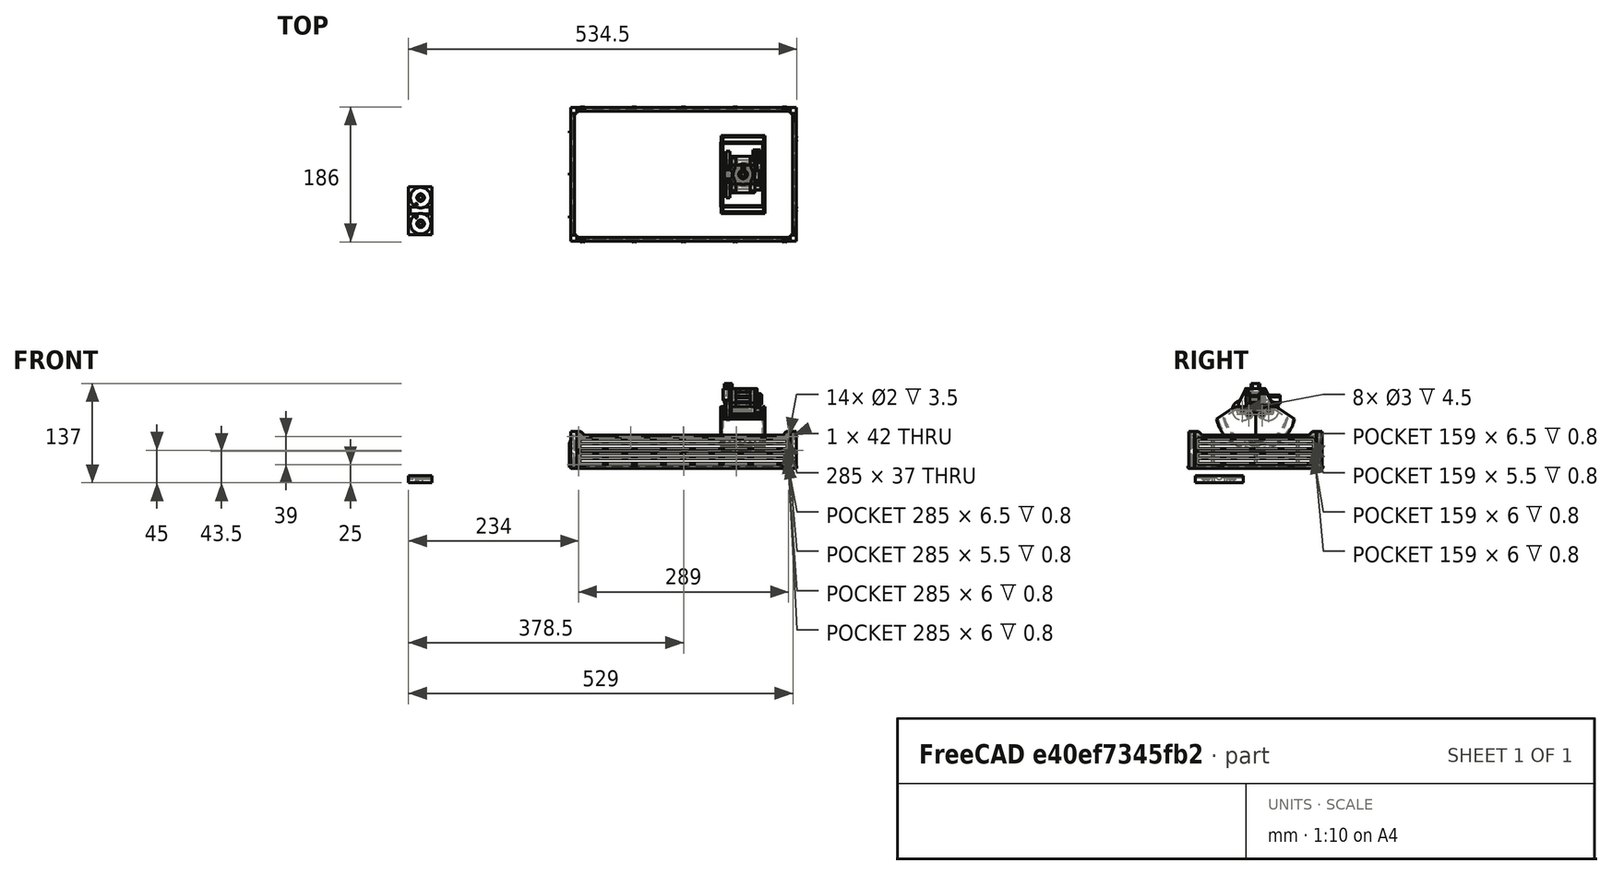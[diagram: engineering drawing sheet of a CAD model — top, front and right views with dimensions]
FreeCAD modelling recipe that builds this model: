
FCSTD DOCUMENT  (FreeCAD 0.18.4R)
Label: bucket
License: All rights reserved
LicenseURL: http://en.wikipedia.org/wiki/All_rights_reserved
objects: Part::Cylinder×157, Part::MultiFuse×80, Part::Cut×78, Part::Box×39, Part::Chamfer×38, Part::Fillet×16, Part::Feature×12, Part::Extrusion×8, Part::Mirroring×4
note: 432 computed .brp shape members not serialized (recipe doc carries the construction recipe); baked Part::Feature solids carry a one-line shape summary decoded from their .brp

FEATURE [Part::Feature] Fusion281001  label="kipper"
  shape: bbox 313 x 186 x 59 mm, 528 faces, 2 solids (baked)
FEATURE [Part::Cylinder] Cylinder002
  Angle = 360
  AttacherType = Attacher::AttachEngine3D
  Height = 5
  Placement = pos=(437,102.5,100) rot=(0,1,0;1.5708rad)
  Radius = 14
FEATURE [Part::Cylinder] Cylinder003
  Angle = 360
  AttacherType = Attacher::AttachEngine3D
  Height = 5
  Placement = pos=(437,67.5,100) rot=(0,1,0;1.5708rad)
  Radius = 14
FEATURE [Part::Cylinder] Cylinder004
  Angle = 360
  AttacherType = Attacher::AttachEngine3D
  Height = 60
  Placement = pos=(432,103,100) rot=(0,1,0;1.5708rad)
  Radius = 1.5
FEATURE [Part::Cylinder] Cylinder005
  Angle = 360
  AttacherType = Attacher::AttachEngine3D
  Height = 60
  Placement = pos=(432,67,100) rot=(0,1,0;1.5708rad)
  Radius = 1.5
FEATURE [Part::Box] Box  label="Cube"
  AttacherType = Attacher::AttachEngine3D
  Height = 10
  Length = 32
  Placement = pos=(446,60,95) rot=(0,0,1;0rad)
  Width = 50
FEATURE [Part::Cylinder] Cylinder1189  label="Cylinder1407"
  Angle = 360
  AttacherType = Attacher::AttachEngine3D
  Height = 27
  Radius = 8
FEATURE [Part::Box] Box501  label="Cube727"
  AttacherType = Attacher::AttachEngine3D
  Height = 27
  Length = 10.4
  Placement = pos=(-5.2,-6.2,0) rot=(0,0,1;0rad)
  Width = 12.4
FEATURE [Part::Cylinder] Cylinder1190  label="Cylinder1408"
  Angle = 360
  AttacherType = Attacher::AttachEngine3D
  Height = 17
  Radius = 8
FEATURE [Part::Cylinder] Cylinder1191  label="Cylinder1409"
  Angle = 360
  AttacherType = Attacher::AttachEngine3D
  Height = 17
  Radius = 6.5
FEATURE [Part::Cut] Cut014239
  Base = -> Cylinder1190
  Refine = true
  Tool = -> Cylinder1191
FEATURE [Part::Fillet] Fillet395
  Base = -> Box501
  Edges = 4 edges r=1: [Edge1,Edge3,Edge5,Edge7]
FEATURE [Part::Cut] Cut014240
  Base = -> Cylinder1189
  Refine = true
  Tool = -> Fillet395
FEATURE [Part::MultiFuse] Fusion248002050121
  Refine = true
  Shapes = -> [Cut014239,Cut014240]
FEATURE [Part::Cylinder] Cylinder1192  label="Cylinder1410"
  Angle = 360
  AttacherType = Attacher::AttachEngine3D
  Height = 27
  Radius = 8
FEATURE [Part::Cut] Cut014241  label="bucket-opening-motor"
  Base = -> Cylinder1192
  Placement = pos=(441.5,85,137) rot=(1,0,0;3.14159rad)
  Refine = true
  Tool = -> Fusion248002050121
FEATURE [Part::Cylinder] Cylinder1193  label="Cylinder1411"
  Angle = 360
  AttacherType = Attacher::AttachEngine3D
  Height = 27
  Radius = 8
FEATURE [Part::Box] Box502  label="Cube728"
  AttacherType = Attacher::AttachEngine3D
  Height = 27
  Length = 10.4
  Placement = pos=(-5.2,-6.2,0) rot=(0,0,1;0rad)
  Width = 12.4
FEATURE [Part::Cylinder] Cylinder1194  label="Cylinder1412"
  Angle = 360
  AttacherType = Attacher::AttachEngine3D
  Height = 17
  Radius = 8
FEATURE [Part::Cylinder] Cylinder1195  label="Cylinder1413"
  Angle = 360
  AttacherType = Attacher::AttachEngine3D
  Height = 17
  Radius = 6.5
FEATURE [Part::Cut] Cut014242
  Base = -> Cylinder1194
  Refine = true
  Tool = -> Cylinder1195
FEATURE [Part::Fillet] Fillet396
  Base = -> Box502
  Edges = 4 edges r=1: [Edge1,Edge3,Edge5,Edge7]
FEATURE [Part::Cut] Cut014243
  Base = -> Cylinder1193
  Refine = true
  Tool = -> Fillet396
FEATURE [Part::MultiFuse] Fusion248002050122
  Refine = true
  Shapes = -> [Cut014242,Cut014243]
FEATURE [Part::Cylinder] Cylinder1196  label="Cylinder1414"
  Angle = 360
  AttacherType = Attacher::AttachEngine3D
  Height = 27
  Radius = 8
FEATURE [Part::Cut] Cut014244  label="bucket-turning-motor"
  Base = -> Cylinder1196
  Placement = pos=(480.5,119,114.75) rot=(1,0,0;1.5708rad)
  Refine = true
  Tool = -> Fusion248002050122
FEATURE [Part::Cylinder] Cylinder1197
  Angle = 360
  AttacherType = Attacher::AttachEngine3D
  Height = 5
  Placement = pos=(462,85,145) rot=(0,0,1;0rad)
  Radius = 14
FEATURE [Part::Cylinder] Cylinder1198
  Angle = 360
  AttacherType = Attacher::AttachEngine3D
  Height = 60
  Placement = pos=(432,94,94) rot=(0,1,0;1.5708rad)
  Radius = 1.5
FEATURE [Part::Cylinder] Cylinder1199
  Angle = 360
  AttacherType = Attacher::AttachEngine3D
  Height = 9.5
  Placement = pos=(434.75,67.5,100) rot=(0,1,0;1.5708rad)
  Radius = 5
FEATURE [Part::Cylinder] Cylinder1200
  Angle = 360
  AttacherType = Attacher::AttachEngine3D
  Height = 9.5
  Placement = pos=(434.75,102.5,100) rot=(0,1,0;1.5708rad)
  Radius = 5
FEATURE [Part::MultiFuse] Fusion
  Placement = pos=(2,-0.5,0) rot=(0,0,1;0rad)
  Refine = true
  Shapes = -> [Cylinder1199,Cylinder003]
FEATURE [Part::MultiFuse] Fusion248002050123
  Placement = pos=(2,0.5,0) rot=(0,0,1;0rad)
  Refine = true
  Shapes = -> [Cylinder002,Cylinder1200]
FEATURE [Part::Cylinder] Cylinder1201
  Angle = 360
  AttacherType = Attacher::AttachEngine3D
  Height = 9.5
  Placement = pos=(462,85,142.75) rot=(0,0,1;0rad)
  Radius = 5
FEATURE [Part::MultiFuse] Fusion248002050124
  Placement = pos=(0,0,-32.75) rot=(0,0,1;0rad)
  Refine = true
  Shapes = -> [Cylinder1197,Cylinder1201]
FEATURE [Part::Cylinder] Cylinder1202
  Angle = 360
  AttacherType = Attacher::AttachEngine3D
  Height = 15
  Placement = pos=(480,92,115) rot=(1,0,0;1.5708rad)
  Radius = 4
FEATURE [Part::Box] Box507  label="Cube733"
  AttacherType = Attacher::AttachEngine3D
  Height = 5
  Length = 22
  Placement = pos=(451,72,125) rot=(0,0,1;0rad)
  Width = 26
FEATURE [Part::Cylinder] Cylinder1203
  Angle = 360
  AttacherType = Attacher::AttachEngine3D
  Height = 10
  Placement = pos=(462,85,110) rot=(0,0,1;0rad)
  Radius = 15
FEATURE [Part::Box] Box508  label="Cube734"
  AttacherType = Attacher::AttachEngine3D
  Height = 10
  Length = 22
  Placement = pos=(462,77,110) rot=(0,0,1;0rad)
  Width = 15
FEATURE [Part::Box] Box506  label="Cube732"
  AttacherType = Attacher::AttachEngine3D
  Height = 25
  Length = 6
  Placement = pos=(472,62,105) rot=(0,0,1;0rad)
  Width = 46
FEATURE [Part::Chamfer] Chamfer005
  Base = -> Box506
  Edges = 2 edges: [Edge10 r1=20 r2=10,Edge12 r1=20 r2=10]
FEATURE [Part::Box] Box509  label="Cube735"
  AttacherType = Attacher::AttachEngine3D
  Height = 25
  Length = 6
  Placement = pos=(472,62,105) rot=(0,0,1;0rad)
  Width = 46
FEATURE [Part::Chamfer] Chamfer006
  Base = -> Box509
  Edges = 2 edges: [Edge10 r1=20 r2=10,Edge12 r1=20 r2=10]
  Placement = pos=(-26,0,0) rot=(0,0,1;0rad)
FEATURE [Part::Cut] Cut014245
  Base = -> Chamfer006
  Refine = true
  Tool = -> Cylinder1203
FEATURE [Part::Cylinder] Cylinder1204  label="Cylinder1415"
  Angle = 360
  AttacherType = Attacher::AttachEngine3D
  Height = 27
  Radius = 8
FEATURE [Part::Box] Box510  label="Cube736"
  AttacherType = Attacher::AttachEngine3D
  Height = 27
  Length = 10.4
  Placement = pos=(-5.2,-6.2,0) rot=(0,0,1;0rad)
  Width = 12.4
FEATURE [Part::Cylinder] Cylinder1205  label="Cylinder1416"
  Angle = 360
  AttacherType = Attacher::AttachEngine3D
  Height = 17
  Radius = 8
FEATURE [Part::Cylinder] Cylinder1206  label="Cylinder1417"
  Angle = 360
  AttacherType = Attacher::AttachEngine3D
  Height = 17
  Radius = 6.5
FEATURE [Part::Cut] Cut014247
  Base = -> Cylinder1205
  Refine = true
  Tool = -> Cylinder1206
FEATURE [Part::Fillet] Fillet398
  Base = -> Box510
  Edges = 4 edges r=1: [Edge1,Edge3,Edge5,Edge7]
FEATURE [Part::Cut] Cut014248
  Base = -> Cylinder1204
  Refine = true
  Tool = -> Fillet398
FEATURE [Part::MultiFuse] Fusion248002050126
  Refine = true
  Shapes = -> [Cut014247,Cut014248]
FEATURE [Part::Cylinder] Cylinder1207  label="Cylinder1418"
  Angle = 360
  AttacherType = Attacher::AttachEngine3D
  Height = 27
  Radius = 8
FEATURE [Part::Cut] Cut014249  label="bucket-opening-motor001"
  Base = -> Cylinder1207
  Placement = pos=(441.5,85,137) rot=(1,0,0;3.14159rad)
  Refine = true
  Tool = -> Fusion248002050126
FEATURE [Part::Cylinder] Cylinder1208  label="Cylinder1419"
  Angle = 360
  AttacherType = Attacher::AttachEngine3D
  Height = 27
  Radius = 8
FEATURE [Part::Box] Box511  label="Cube737"
  AttacherType = Attacher::AttachEngine3D
  Height = 27
  Length = 10.4
  Placement = pos=(-5.2,-6.2,0) rot=(0,0,1;0rad)
  Width = 12.4
FEATURE [Part::Cylinder] Cylinder1209  label="Cylinder1420"
  Angle = 360
  AttacherType = Attacher::AttachEngine3D
  Height = 17
  Radius = 8
FEATURE [Part::Cylinder] Cylinder1210  label="Cylinder1421"
  Angle = 360
  AttacherType = Attacher::AttachEngine3D
  Height = 17
  Radius = 6.5
FEATURE [Part::Cut] Cut014250
  Base = -> Cylinder1209
  Refine = true
  Tool = -> Cylinder1210
FEATURE [Part::Fillet] Fillet399
  Base = -> Box511
  Edges = 4 edges r=1: [Edge1,Edge3,Edge5,Edge7]
FEATURE [Part::Cut] Cut014251
  Base = -> Cylinder1208
  Refine = true
  Tool = -> Fillet399
FEATURE [Part::MultiFuse] Fusion248002050127
  Refine = true
  Shapes = -> [Cut014250,Cut014251]
FEATURE [Part::Cylinder] Cylinder1211  label="Cylinder1422"
  Angle = 360
  AttacherType = Attacher::AttachEngine3D
  Height = 27
  Radius = 8
FEATURE [Part::Cut] Cut014252  label="bucket-turning-motor001"
  Base = -> Cylinder1211
  Placement = pos=(480.5,119,114.75) rot=(1,0,0;1.5708rad)
  Refine = true
  Tool = -> Fusion248002050127
FEATURE [Part::Box] Box513  label="Cube739"
  AttacherType = Attacher::AttachEngine3D
  Height = 21
  Length = 6
  Placement = pos=(441,77.5,109) rot=(0,0,1;0rad)
  Width = 15
FEATURE [Part::Cylinder] Cylinder1212
  Angle = 360
  AttacherType = Attacher::AttachEngine3D
  Height = 15
  Placement = pos=(441.5,85,94) rot=(0,0,1;0rad)
  Radius = 4.75
FEATURE [Part::Cylinder] Cylinder1213
  Angle = 360
  AttacherType = Attacher::AttachEngine3D
  Height = 16
  Placement = pos=(441.5,85,94) rot=(0,0,1;0rad)
  Radius = 5.5
FEATURE [Part::Cut] Cut014255
  Base = -> Cut014245
  Refine = true
  Tool = -> Cylinder1213
FEATURE [Part::Cylinder] Cylinder1214
  Angle = 360
  AttacherType = Attacher::AttachEngine3D
  Height = 16
  Placement = pos=(441.5,85,94) rot=(0,0,1;0rad)
  Radius = 5.5
FEATURE [Part::Chamfer] Chamfer007
  Base = -> Box513
  Edges = 2 edges r=1.5: [Edge9,Edge11]
FEATURE [Part::Cylinder] Cylinder1215
  Angle = 360
  AttacherType = Attacher::AttachEngine3D
  Height = 16
  Placement = pos=(441.5,85,94) rot=(0,0,1;0rad)
  Radius = 2
FEATURE [Part::Cut] Cut014257
  Base = -> Chamfer007
  Refine = true
  Tool = -> Cylinder1215
FEATURE [Part::MultiFuse] Fusion248002050128
  Refine = true
  Shapes = -> [Cut014255,Cut014257]
FEATURE [Part::Cut] Cut014258
  Base = -> Fusion248002050128
  Refine = true
  Tool = -> Cut014249
FEATURE [Part::Cylinder] Cylinder1216
  Angle = 360
  AttacherType = Attacher::AttachEngine3D
  Height = 10
  Placement = pos=(462,85,110) rot=(0,0,1;0rad)
  Radius = 15
FEATURE [Part::Cut] Cut014259
  Base = -> Chamfer005
  Refine = true
  Tool = -> Cylinder1216
FEATURE [Part::Cut] Cut014260
  Base = -> Cut014259
  Refine = true
  Tool = -> Box508
FEATURE [Part::Cut] Cut014261
  Base = -> Cut014260
  Refine = true
  Tool = -> Cut014252
FEATURE [Part::Cylinder] Cylinder1217
  Angle = 360
  AttacherType = Attacher::AttachEngine3D
  Height = 15
  Placement = pos=(480,87,115) rot=(1,0,0;1.5708rad)
  Radius = 1.6
FEATURE [Part::MultiFuse] Fusion248002050129
  Placement = pos=(0.5,0,0) rot=(0,0,1;0rad)
  Refine = true
  Shapes = -> [Cylinder1202,Cylinder1217]
FEATURE [Part::Box] Box514  label="Cube740"
  AttacherType = Attacher::AttachEngine3D
  Height = 12
  Length = 7.5
  Placement = pos=(478,72,109) rot=(0,0,1;0rad)
  Width = 5
FEATURE [Part::Cylinder] Cylinder1218
  Angle = 360
  AttacherType = Attacher::AttachEngine3D
  Height = 5
  Placement = pos=(480.5,77,115) rot=(1,0,0;1.5708rad)
  Radius = 3.1
FEATURE [Part::Box] Box515  label="Cube741"
  AttacherType = Attacher::AttachEngine3D
  Height = 21
  Length = 6
  Placement = pos=(441,77.5,109) rot=(0,0,1;0rad)
  Width = 15
FEATURE [Part::Box] Box516  label="Cube742"
  AttacherType = Attacher::AttachEngine3D
  Height = 16
  Length = 3
  Placement = pos=(443,71.5,114) rot=(0,0,1;0rad)
  Width = 27
FEATURE [Part::Cylinder] Cylinder1219  label="Cylinder1423"
  Angle = 360
  AttacherType = Attacher::AttachEngine3D
  Height = 27
  Radius = 8
FEATURE [Part::Box] Box517  label="Cube743"
  AttacherType = Attacher::AttachEngine3D
  Height = 27
  Length = 10.4
  Placement = pos=(-5.2,-6.2,0) rot=(0,0,1;0rad)
  Width = 12.4
FEATURE [Part::Cylinder] Cylinder1220  label="Cylinder1424"
  Angle = 360
  AttacherType = Attacher::AttachEngine3D
  Height = 17
  Radius = 8
FEATURE [Part::Cylinder] Cylinder1221  label="Cylinder1425"
  Angle = 360
  AttacherType = Attacher::AttachEngine3D
  Height = 17
  Radius = 6.5
FEATURE [Part::Cut] Cut014263
  Base = -> Cylinder1220
  Refine = true
  Tool = -> Cylinder1221
FEATURE [Part::Fillet] Fillet401
  Base = -> Box517
  Edges = 4 edges r=1: [Edge1,Edge3,Edge5,Edge7]
FEATURE [Part::Cut] Cut014264
  Base = -> Cylinder1219
  Refine = true
  Tool = -> Fillet401
FEATURE [Part::MultiFuse] Fusion248002050131
  Refine = true
  Shapes = -> [Cut014263,Cut014264]
FEATURE [Part::Cylinder] Cylinder1222  label="Cylinder1426"
  Angle = 360
  AttacherType = Attacher::AttachEngine3D
  Height = 27
  Radius = 8
FEATURE [Part::Cut] Cut014265  label="bucket-opening-motor002"
  Base = -> Cylinder1222
  Placement = pos=(441.5,85,137) rot=(1,0,0;3.14159rad)
  Refine = true
  Tool = -> Fusion248002050131
FEATURE [Part::MultiFuse] Fusion248002050132
  Refine = true
  Shapes = -> [Box515,Cut014265]
FEATURE [Part::Box] Box518  label="Cube744"
  AttacherType = Attacher::AttachEngine3D
  Height = 16
  Length = 12
  Placement = pos=(434,76.5,114) rot=(0,0,1;0rad)
  Width = 17
FEATURE [Part::Cylinder] Cylinder1223
  Angle = 360
  AttacherType = Attacher::AttachEngine3D
  Height = 11
  Placement = pos=(439,96,121) rot=(0,1,0;1.5708rad)
  Radius = 1.2
FEATURE [Part::Cylinder] Cylinder1224
  Angle = 360
  AttacherType = Attacher::AttachEngine3D
  Height = 11
  Placement = pos=(439,74,121) rot=(0,1,0;1.5708rad)
  Radius = 1.2
FEATURE [Part::Cylinder] Cylinder1225
  Angle = 360
  AttacherType = Attacher::AttachEngine3D
  Height = 11
  Placement = pos=(439,74,121) rot=(0,1,0;1.5708rad)
  Radius = 1
FEATURE [Part::Cylinder] Cylinder1226
  Angle = 360
  AttacherType = Attacher::AttachEngine3D
  Height = 11
  Placement = pos=(439,96,121) rot=(0,1,0;1.5708rad)
  Radius = 1
FEATURE [Part::MultiFuse] Fusion248002050134
  Placement = pos=(0,0,-4) rot=(0,0,1;0rad)
  Refine = true
  Shapes = -> [Cylinder1224,Cylinder1223]
FEATURE [Part::MultiFuse] Fusion248002050135
  Refine = true
  Shapes = -> [Cylinder1225,Cylinder1226]
FEATURE [Part::Box] Box519  label="Cube745"
  AttacherType = Attacher::AttachEngine3D
  Height = 16
  Length = 9.5
  Placement = pos=(478,90,107) rot=(0,0,1;0rad)
  Width = 18
FEATURE [Part::Cylinder] Cylinder1228
  Angle = 360
  AttacherType = Attacher::AttachEngine3D
  Height = 11
  Placement = pos=(476,96,128) rot=(0,1,0;1.5708rad)
  Radius = 1.2
FEATURE [Part::Cylinder] Cylinder1229
  Angle = 360
  AttacherType = Attacher::AttachEngine3D
  Height = 11
  Placement = pos=(476,95,105) rot=(0,1,0;1.5708rad)
  Radius = 1.2
FEATURE [Part::Cylinder] Cylinder1230
  Angle = 360
  AttacherType = Attacher::AttachEngine3D
  Height = 15
  Placement = pos=(480,92,115) rot=(1,0,0;1.5708rad)
  Radius = 5.5
FEATURE [Part::Cylinder] Cylinder1231  label="Cylinder1427"
  Angle = 360
  AttacherType = Attacher::AttachEngine3D
  Height = 27
  Radius = 8
FEATURE [Part::Box] Box520  label="Cube746"
  AttacherType = Attacher::AttachEngine3D
  Height = 27
  Length = 10.4
  Placement = pos=(-5.2,-6.2,0) rot=(0,0,1;0rad)
  Width = 12.4
FEATURE [Part::Cylinder] Cylinder1232  label="Cylinder1428"
  Angle = 360
  AttacherType = Attacher::AttachEngine3D
  Height = 17
  Radius = 8
FEATURE [Part::Cylinder] Cylinder1233  label="Cylinder1429"
  Angle = 360
  AttacherType = Attacher::AttachEngine3D
  Height = 17
  Radius = 6.5
FEATURE [Part::Cut] Cut014270
  Base = -> Cylinder1232
  Refine = true
  Tool = -> Cylinder1233
FEATURE [Part::Fillet] Fillet403
  Base = -> Box520
  Edges = 4 edges r=1: [Edge1,Edge3,Edge5,Edge7]
FEATURE [Part::Cut] Cut014271
  Base = -> Cylinder1231
  Refine = true
  Tool = -> Fillet403
FEATURE [Part::MultiFuse] Fusion248002050137
  Refine = true
  Shapes = -> [Cut014270,Cut014271]
FEATURE [Part::Cylinder] Cylinder1234  label="Cylinder1430"
  Angle = 360
  AttacherType = Attacher::AttachEngine3D
  Height = 27
  Radius = 8
FEATURE [Part::Cut] Cut014272  label="bucket-turning-motor002"
  Base = -> Cylinder1234
  Placement = pos=(480.5,119,114.75) rot=(1,0,0;1.5708rad)
  Refine = true
  Tool = -> Fusion248002050137
FEATURE [Part::Cylinder] Cylinder1235
  Angle = 360
  AttacherType = Attacher::AttachEngine3D
  Height = 5
  Placement = pos=(473,95,105) rot=(0,1,0;1.5708rad)
  Radius = 1
FEATURE [Part::Box] Box521  label="Cube747"
  AttacherType = Attacher::AttachEngine3D
  Height = 6
  Length = 5
  Placement = pos=(434,78,42) rot=(0,0,1;0rad)
  Width = 20
FEATURE [Part::Cylinder] Cylinder1243
  Angle = 80
  AttacherType = Attacher::AttachEngine3D
  Height = 60
  Placement = pos=(432,85,100) rot=(0,1,0;1.5708rad)
  Radius = 55
FEATURE [Part::Box] Box522  label="Cube748"
  AttacherType = Attacher::AttachEngine3D
  Height = 6
  Length = 10
  Placement = pos=(434,65,44.75) rot=(0,0,1;0rad)
  Width = 20
FEATURE [Part::MultiFuse] Fusion248002050143
  Refine = true
  Shapes = -> [Box522,Cylinder1243]
FEATURE [Part::Cut] Cut014276
  Base = -> Box521
  Refine = true
  Tool = -> Fusion248002050143
FEATURE [Part::Chamfer] Chamfer012
  Base = -> Cut014276
  Edges = 1 edges: [Edge17 r1=3 r2=8]
FEATURE [Part::Chamfer] Chamfer013
  Base = -> Chamfer012
  Edges = 1 edges: [Edge15 r1=11 r2=2]
  Placement = pos=(1,0,9) rot=(0,0,1;0rad)
FEATURE [Part::Box] Box523  label="Cube749"
  AttacherType = Attacher::AttachEngine3D
  Height = 6
  Length = 5
  Placement = pos=(434,78,42) rot=(0,0,1;0rad)
  Width = 20
FEATURE [Part::Cylinder] Cylinder1244
  Angle = 80
  AttacherType = Attacher::AttachEngine3D
  Height = 60
  Placement = pos=(432,85,100) rot=(0,1,0;1.5708rad)
  Radius = 55
FEATURE [Part::Box] Box524  label="Cube750"
  AttacherType = Attacher::AttachEngine3D
  Height = 6
  Length = 10
  Placement = pos=(434,65,44.75) rot=(0,0,1;0rad)
  Width = 20
FEATURE [Part::MultiFuse] Fusion248002050144
  Refine = true
  Shapes = -> [Box524,Cylinder1244]
FEATURE [Part::Cut] Cut014277
  Base = -> Box523
  Refine = true
  Tool = -> Fusion248002050144
FEATURE [Part::Chamfer] Chamfer014
  Base = -> Cut014277
  Edges = 1 edges: [Edge17 r1=3 r2=8]
FEATURE [Part::Chamfer] Chamfer015
  Base = -> Chamfer014
  Edges = 1 edges: [Edge15 r1=11 r2=2]
  Placement = pos=(29,0,9) rot=(0,0,1;0rad)
FEATURE [Part::Box] Box525  label="Cube751"
  AttacherType = Attacher::AttachEngine3D
  Height = 6
  Length = 5
  Placement = pos=(434,78,42) rot=(0,0,1;0rad)
  Width = 20
FEATURE [Part::Cylinder] Cylinder1245
  Angle = 80
  AttacherType = Attacher::AttachEngine3D
  Height = 60
  Placement = pos=(432,85,100) rot=(0,1,0;1.5708rad)
  Radius = 55
FEATURE [Part::Box] Box526  label="Cube752"
  AttacherType = Attacher::AttachEngine3D
  Height = 6
  Length = 10
  Placement = pos=(434,65,44.75) rot=(0,0,1;0rad)
  Width = 20
FEATURE [Part::MultiFuse] Fusion248002050145
  Refine = true
  Shapes = -> [Box526,Cylinder1245]
FEATURE [Part::Cut] Cut014278
  Base = -> Box525
  Refine = true
  Tool = -> Fusion248002050145
FEATURE [Part::Chamfer] Chamfer016
  Base = -> Cut014278
  Edges = 1 edges: [Edge17 r1=3 r2=8]
FEATURE [Part::Chamfer] Chamfer017
  Base = -> Chamfer016
  Edges = 1 edges: [Edge15 r1=11 r2=2]
  Placement = pos=(15,0,9) rot=(0,0,1;0rad)
FEATURE [Part::Box] Box527  label="Cube753"
  AttacherType = Attacher::AttachEngine3D
  Height = 6
  Length = 5
  Placement = pos=(434,78,42) rot=(0,0,1;0rad)
  Width = 20
FEATURE [Part::Cylinder] Cylinder1246
  Angle = 80
  AttacherType = Attacher::AttachEngine3D
  Height = 60
  Placement = pos=(432,85,100) rot=(0,1,0;1.5708rad)
  Radius = 55
FEATURE [Part::Box] Box528  label="Cube754"
  AttacherType = Attacher::AttachEngine3D
  Height = 6
  Length = 10
  Placement = pos=(434,65,44.75) rot=(0,0,1;0rad)
  Width = 20
FEATURE [Part::MultiFuse] Fusion248002050146
  Refine = true
  Shapes = -> [Box528,Cylinder1246]
FEATURE [Part::Cut] Cut014279
  Base = -> Box527
  Refine = true
  Tool = -> Fusion248002050146
FEATURE [Part::Chamfer] Chamfer018
  Base = -> Cut014279
  Edges = 1 edges: [Edge17 r1=3 r2=8]
FEATURE [Part::Chamfer] Chamfer019
  Base = -> Chamfer018
  Edges = 1 edges: [Edge15 r1=11 r2=2]
  Placement = pos=(43,0,9) rot=(0,0,1;0rad)
FEATURE [Part::Cylinder] Cylinder1259
  Angle = 360
  AttacherType = Attacher::AttachEngine3D
  Height = 60
  Placement = pos=(432,76,94) rot=(0,1,0;1.5708rad)
  Radius = 1.5
FEATURE [Part::Cylinder] Cylinder1272  label="Cylinder1443"
  Angle = 360
  AttacherType = Attacher::AttachEngine3D
  Height = 10
  Placement = pos=(436.5,89.5,42.3) rot=(0,0,1;0rad)
  Radius = 0.8
FEATURE [Part::Box] Box539  label="Cube765"
  AttacherType = Attacher::AttachEngine3D
  Height = 6
  Length = 5
  Placement = pos=(434,78,42) rot=(0,0,1;0rad)
  Width = 20
FEATURE [Part::Cylinder] Cylinder1273
  Angle = 80
  AttacherType = Attacher::AttachEngine3D
  Height = 60
  Placement = pos=(432,85,100) rot=(0,1,0;1.5708rad)
  Radius = 55
FEATURE [Part::Box] Box540  label="Cube766"
  AttacherType = Attacher::AttachEngine3D
  Height = 6
  Length = 10
  Placement = pos=(434,65,44.75) rot=(0,0,1;0rad)
  Width = 20
FEATURE [Part::MultiFuse] Fusion248002050161
  Refine = true
  Shapes = -> [Box540,Cylinder1273]
FEATURE [Part::Cut] Cut014288
  Base = -> Box539
  Refine = true
  Tool = -> Fusion248002050161
FEATURE [Part::Chamfer] Chamfer034
  Base = -> Cut014288
  Edges = 1 edges: [Edge17 r1=3 r2=8]
FEATURE [Part::Chamfer] Chamfer035
  Base = -> Chamfer034
  Edges = 1 edges: [Edge15 r1=11 r2=2]
FEATURE [Part::Cut] Cut014289  label="bucket-tooth"
  Base = -> Chamfer035
  Refine = true
  Tool = -> Cylinder1272
FEATURE [Part::MultiFuse] Fusion248002050162
  Refine = true
  Shapes = -> [Box518,Box516]
FEATURE [Part::Fillet] Fillet406
  Base = -> Fusion248002050162
  Edges = 4 edges r=3: [Edge17,Edge19,Edge20,Edge22]
FEATURE [Part::Fillet] Fillet407
  Base = -> Fillet406
  Edges = 2 edges r=4: [Edge17,Edge30]
FEATURE [Part::Cut] Cut014290
  Base = -> Fillet407
  Refine = true
  Tool = -> Fusion248002050132
FEATURE [Part::Cut] Cut014291
  Base = -> Cut014290
  Refine = true
  Tool = -> Fusion248002050134
FEATURE [Part::Cut] Cut014292
  Base = -> Cut014258
  Refine = true
  Tool = -> Fusion248002050135
FEATURE [Part::Chamfer] Chamfer036
  Base = -> Box519
  Edges = 1 edges: [Edge12 r1=13 r2=6.5]
FEATURE [Part::Fillet] Fillet409
  Base = -> Chamfer036
  Edges = 2 edges r=2.5: [Edge8,Edge15]
FEATURE [Part::Cylinder] Cylinder1275
  Angle = 360
  AttacherType = Attacher::AttachEngine3D
  Height = 11
  Placement = pos=(481,95,105) rot=(0,1,0;1.5708rad)
  Radius = 2.3
FEATURE [Part::Box] Box542  label="Cube768"
  AttacherType = Attacher::AttachEngine3D
  Height = 28
  Length = 3
  Placement = pos=(478,92,102) rot=(0,0,1;0rad)
  Width = 7
FEATURE [Part::Cylinder] Cylinder1284
  Angle = 360
  AttacherType = Attacher::AttachEngine3D
  Height = 60
  Placement = pos=(432,76.5,94) rot=(0,1,0;1.5708rad)
  Radius = 3
FEATURE [Part::Cylinder] Cylinder1285
  Angle = 360
  AttacherType = Attacher::AttachEngine3D
  Height = 60
  Placement = pos=(432,93.5,94) rot=(0,1,0;1.5708rad)
  Radius = 3
FEATURE [Part::MultiFuse] Fusion248002050169
  Refine = true
  Shapes = -> [Cylinder1284,Cylinder1285]
FEATURE [Part::Cylinder] Cylinder1286
  Angle = 360
  AttacherType = Attacher::AttachEngine3D
  Height = 6.5
  Placement = pos=(462,85,125) rot=(0,0,1;0rad)
  Radius = 6
FEATURE [Part::Cylinder] Cylinder1287
  Angle = 360
  AttacherType = Attacher::AttachEngine3D
  Height = 4.5
  Placement = pos=(462,85,105.5) rot=(0,0,1;0rad)
  Radius = 5.6
FEATURE [Part::Cylinder] Cylinder1288
  Angle = 360
  AttacherType = Attacher::AttachEngine3D
  Height = 5
  Placement = pos=(462,85,105) rot=(0,0,1;0rad)
  Radius = 10
FEATURE [Part::Cut] Cut014299
  Base = -> Cylinder1288
  Refine = true
  Tool = -> Cylinder1287
FEATURE [Part::Cylinder] Cylinder1289
  Angle = 360
  AttacherType = Attacher::AttachEngine3D
  Height = 33.5
  Placement = pos=(462,85,93.75) rot=(0,0,1;0rad)
  Radius = 3
FEATURE [Part::Cylinder] Cylinder1290
  Angle = 360
  AttacherType = Attacher::AttachEngine3D
  Height = 6
  Placement = pos=(462,85,119.5) rot=(0,0,1;0rad)
  Radius = 10
FEATURE [Part::Cylinder] Cylinder1291
  Angle = 360
  AttacherType = Attacher::AttachEngine3D
  Height = 4.5
  Placement = pos=(462,85,119.5) rot=(0,0,1;0rad)
  Radius = 5.6
FEATURE [Part::Cut] Cut014301
  Base = -> Cylinder1290
  Refine = true
  Tool = -> Cylinder1291
FEATURE [Part::MultiFuse] Fusion248002050171
  Refine = true
  Shapes = -> [Box507,Cut014301]
FEATURE [Part::Cylinder] Cylinder1292
  Angle = 360
  AttacherType = Attacher::AttachEngine3D
  Height = 6.5
  Placement = pos=(462,85,123) rot=(0,0,1;0rad)
  Radius = 3
FEATURE [Part::Cylinder] Cylinder1293
  Angle = 360
  AttacherType = Attacher::AttachEngine3D
  Height = 11
  Placement = pos=(462,88,128) rot=(-1,0,0;1.5708rad)
  Radius = 2
FEATURE [Part::Box] Box543  label="Cube769"
  AttacherType = Attacher::AttachEngine3D
  Height = 4
  Length = 4
  Placement = pos=(460,88,128) rot=(0,0,1;0rad)
  Width = 11
FEATURE [Part::MultiFuse] Fusion248002050172
  Refine = true
  Shapes = -> [Cylinder1293,Box543]
FEATURE [Part::Cylinder] Cylinder1294
  Angle = 360
  AttacherType = Attacher::AttachEngine3D
  Height = 60
  Placement = pos=(432,103,100) rot=(0,1,0;1.5708rad)
  Radius = 2.5
FEATURE [Part::Cylinder] Cylinder1295
  Angle = 360
  AttacherType = Attacher::AttachEngine3D
  Height = 60
  Placement = pos=(432,67,100) rot=(0,1,0;1.5708rad)
  Radius = 2.5
FEATURE [Part::MultiFuse] Fusion248002050173
  Refine = true
  Shapes = -> [Cylinder1294,Cylinder1295]
FEATURE [Part::Cylinder] Cylinder1296
  Angle = 360
  AttacherType = Attacher::AttachEngine3D
  Height = 8
  Placement = pos=(432,103,100) rot=(0,1,0;1.5708rad)
  Radius = 4
FEATURE [Part::Cylinder] Cylinder1297
  Angle = 360
  AttacherType = Attacher::AttachEngine3D
  Height = 8
  Placement = pos=(432,67,100) rot=(0,1,0;1.5708rad)
  Radius = 4
FEATURE [Part::MultiFuse] Fusion248002050174
  Placement = pos=(14,0,0) rot=(0,0,1;0rad)
  Refine = true
  Shapes = -> [Cylinder1296,Cylinder1297]
FEATURE [Part::Cylinder] Cylinder1310
  Angle = 360
  AttacherType = Attacher::AttachEngine3D
  Height = 5
  Placement = pos=(462,85,125) rot=(0,0,1;0rad)
  Radius = 13.75
FEATURE [Part::Cylinder] Cylinder1311
  Angle = 360
  AttacherType = Attacher::AttachEngine3D
  Height = 19
  Placement = pos=(462,85,112) rot=(0,0,1;0rad)
  Radius = 14
FEATURE [Part::Box] Box544  label="Cube770"
  AttacherType = Attacher::AttachEngine3D
  Height = 5
  Length = 22.5
  Placement = pos=(450.75,71.75,125) rot=(0,0,1;0rad)
  Width = 26.5
FEATURE [Part::MultiFuse] Fusion248002050186
  Refine = true
  Shapes = -> [Fusion248002050171,Cylinder1310]
FEATURE [Part::Cut] Cut014314
  Base = -> Fusion248002050186
  Refine = true
  Tool = -> Cylinder1286
FEATURE [Part::Cut] Cut014315
  Base = -> Cut014314
  Refine = true
  Tool = -> Cylinder1292
FEATURE [Part::Cut] Cut014316
  Base = -> Cut014315
  Refine = true
  Tool = -> Fusion248002050172
FEATURE [Part::MultiFuse] Fusion248002050187
  Refine = true
  Shapes = -> [Cylinder004,Cylinder005,Cylinder1198,Cylinder1259]
FEATURE [Part::Cylinder] Cylinder1313
  Angle = 360
  AttacherType = Attacher::AttachEngine3D
  Height = 11
  Placement = pos=(439,96,121) rot=(0,1,0;1.5708rad)
  Radius = 1.2
FEATURE [Part::Cylinder] Cylinder1314
  Angle = 360
  AttacherType = Attacher::AttachEngine3D
  Height = 11
  Placement = pos=(439,74,121) rot=(0,1,0;1.5708rad)
  Radius = 1.2
FEATURE [Part::MultiFuse] Fusion248002050188
  Placement = pos=(0,0,7) rot=(0,0,1;0rad)
  Refine = true
  Shapes = -> [Cylinder1314,Cylinder1313]
FEATURE [Part::Cut] Cut014317  label="bucket-opening-motor-holder"
  Base = -> Cut014291
  Refine = true
  Tool = -> Fusion248002050188
FEATURE [Part::Cylinder] Cylinder1315
  Angle = 360
  AttacherType = Attacher::AttachEngine3D
  Height = 11
  Placement = pos=(439,96,121) rot=(0,1,0;1.5708rad)
  Radius = 1.2
FEATURE [Part::Cylinder] Cylinder1316
  Angle = 360
  AttacherType = Attacher::AttachEngine3D
  Height = 11
  Placement = pos=(439,74,121) rot=(0,1,0;1.5708rad)
  Radius = 1.2
FEATURE [Part::MultiFuse] Fusion248002050189
  Placement = pos=(7,0,7) rot=(0,0,1;0rad)
  Refine = true
  Shapes = -> [Cylinder1316,Cylinder1315]
FEATURE [Part::Cylinder] Cylinder1317
  Angle = 360
  AttacherType = Attacher::AttachEngine3D
  Height = 7
  Placement = pos=(439,96,121) rot=(0,1,0;1.5708rad)
  Radius = 1
FEATURE [Part::Cylinder] Cylinder1318
  Angle = 360
  AttacherType = Attacher::AttachEngine3D
  Height = 7
  Placement = pos=(439,74,121) rot=(0,1,0;1.5708rad)
  Radius = 1
FEATURE [Part::MultiFuse] Fusion248002050190
  Placement = pos=(12,0,7) rot=(0,0,1;0rad)
  Refine = true
  Shapes = -> [Cylinder1318,Cylinder1317]
FEATURE [Part::Cylinder] Cylinder1319
  Angle = 360
  AttacherType = Attacher::AttachEngine3D
  Height = 7
  Placement = pos=(439,96,121) rot=(0,1,0;1.5708rad)
  Radius = 1
FEATURE [Part::Cylinder] Cylinder1320
  Angle = 360
  AttacherType = Attacher::AttachEngine3D
  Height = 7
  Placement = pos=(439,74,121) rot=(0,1,0;1.5708rad)
  Radius = 1
FEATURE [Part::MultiFuse] Fusion248002050191
  Placement = pos=(27,0,7) rot=(0,0,1;0rad)
  Refine = true
  Shapes = -> [Cylinder1320,Cylinder1319]
FEATURE [Part::MultiFuse] Fusion248002050192
  Refine = true
  Shapes = -> [Fusion248002050191,Fusion248002050190]
FEATURE [Part::Cut] Cut014318  label="bucket-head"
  Base = -> Cut014316
  Refine = true
  Tool = -> Fusion248002050192
FEATURE [Part::Cylinder] Cylinder1321
  Angle = 360
  AttacherType = Attacher::AttachEngine3D
  Height = 11
  Placement = pos=(439,96,121) rot=(0,1,0;1.5708rad)
  Radius = 1.2
FEATURE [Part::Cylinder] Cylinder1322
  Angle = 360
  AttacherType = Attacher::AttachEngine3D
  Height = 11
  Placement = pos=(439,74,121) rot=(0,1,0;1.5708rad)
  Radius = 1.2
FEATURE [Part::MultiFuse] Fusion248002050193
  Placement = pos=(28,0,7) rot=(0,0,1;0rad)
  Refine = true
  Shapes = -> [Cylinder1322,Cylinder1321]
FEATURE [Part::MultiFuse] Fusion248002050194
  Refine = true
  Shapes = -> [Fusion248002050189,Fusion248002050193]
FEATURE [Part::MultiFuse] Fusion248002050197
  Refine = true
  Shapes = -> [Cylinder1228,Cylinder1229]
FEATURE [Part::Cylinder] Cylinder1323
  Angle = 360
  AttacherType = Attacher::AttachEngine3D
  Height = 5
  Placement = pos=(437,102.5,100) rot=(0,1,0;1.5708rad)
  Radius = 14.1
FEATURE [Part::Cylinder] Cylinder1324
  Angle = 360
  AttacherType = Attacher::AttachEngine3D
  Height = 5
  Placement = pos=(437,67.5,100) rot=(0,1,0;1.5708rad)
  Radius = 14.1
FEATURE [Part::Cylinder] Cylinder1325
  Angle = 360
  AttacherType = Attacher::AttachEngine3D
  Height = 9.5
  Placement = pos=(434.75,67.5,100) rot=(0,1,0;1.5708rad)
  Radius = 5.2
FEATURE [Part::Cylinder] Cylinder1326
  Angle = 360
  AttacherType = Attacher::AttachEngine3D
  Height = 9.5
  Placement = pos=(434.75,102.5,100) rot=(0,1,0;1.5708rad)
  Radius = 5.2
FEATURE [Part::MultiFuse] Fusion248002050198
  Placement = pos=(2,-0.5,0) rot=(0,0,1;0rad)
  Refine = true
  Shapes = -> [Cylinder1325,Cylinder1324]
FEATURE [Part::MultiFuse] Fusion248002050199
  Placement = pos=(2,0.5,0) rot=(0,0,1;0rad)
  Refine = true
  Shapes = -> [Cylinder1323,Cylinder1326]
FEATURE [Part::Cylinder] Cylinder1327
  Angle = 360
  AttacherType = Attacher::AttachEngine3D
  Height = 27
  Placement = pos=(441.5,85,87) rot=(0,0,1;0rad)
  Radius = 4.75
FEATURE [Part::Cylinder] Cylinder1328
  Angle = 360
  AttacherType = Attacher::AttachEngine3D
  Height = 15
  Placement = pos=(428.75,67,100) rot=(0,1,0;1.5708rad)
  Radius = 2.7
FEATURE [Part::Cylinder] Cylinder1329
  Angle = 360
  AttacherType = Attacher::AttachEngine3D
  Height = 15
  Placement = pos=(428.75,103,100) rot=(0,1,0;1.5708rad)
  Radius = 2.7
FEATURE [Part::Box] Box545  label="Cube771"
  AttacherType = Attacher::AttachEngine3D
  Height = 10
  Length = 32
  Placement = pos=(1.5,2,0) rot=(0,0,1;0rad)
  Width = 66
FEATURE [Part::Cylinder] Cylinder1330
  Angle = 360
  AttacherType = Attacher::AttachEngine3D
  Height = 60
  Placement = pos=(432,103,100) rot=(0,1,0;1.5708rad)
  Radius = 1.6
FEATURE [Part::Cylinder] Cylinder1331
  Angle = 360
  AttacherType = Attacher::AttachEngine3D
  Height = 60
  Placement = pos=(432,67,100) rot=(0,1,0;1.5708rad)
  Radius = 1.6
FEATURE [Part::Cylinder] Cylinder1332
  Angle = 360
  AttacherType = Attacher::AttachEngine3D
  Height = 60
  Placement = pos=(432,93.5,94) rot=(0,1,0;1.5708rad)
  Radius = 1.6
FEATURE [Part::Cylinder] Cylinder1333
  Angle = 360
  AttacherType = Attacher::AttachEngine3D
  Height = 60
  Placement = pos=(432,76.5,94) rot=(0,1,0;1.5708rad)
  Radius = 1.6
FEATURE [Part::MultiFuse] Fusion248002050200
  Placement = pos=(-82,-50,452) rot=(0,1,0;1.5708rad)
  Refine = true
  Shapes = -> [Cylinder1330,Cylinder1331,Cylinder1332,Cylinder1333]
FEATURE [Part::MultiFuse] Fusion248002050201
  Placement = pos=(118,-50,-432) rot=(0,-1,0;1.5708rad)
  Refine = true
  Shapes = -> [Fusion248002050198,Cylinder1329,Cylinder1328,Cylinder1327,Fusion248002050199]
FEATURE [Part::MultiFuse] Fusion248002050202
  Refine = true
  Shapes = -> [Cylinder1311,Box544]
FEATURE [Part::Cut] Cut014325
  Base = -> Box
  Refine = true
  Tool = -> Cylinder1214
FEATURE [Part::Cut] Cut014326
  Base = -> Cut014325
  Refine = true
  Tool = -> Fusion248002050169
FEATURE [Part::MultiFuse] Fusion248002050203
  Refine = true
  Shapes = -> [Cut014326,Cut014299]
FEATURE [Part::Cut] Cut014327
  Base = -> Fusion248002050203
  Refine = true
  Tool = -> Cylinder1289
FEATURE [Part::Cut] Cut014328
  Base = -> Cut014327
  Refine = true
  Tool = -> Fusion248002050173
FEATURE [Part::Cut] Cut014329
  Base = -> Cut014328
  Refine = true
  Tool = -> Fusion248002050174
FEATURE [Part::Fillet] Fillet413
  Base = -> Cut014329
  Edges = 4 edges r=2: [Edge8,Edge12,Edge15,Edge35]
FEATURE [Part::MultiFuse] Fusion248002050204
  Refine = true
  Shapes = -> [Box514,Cut014261]
FEATURE [Part::Chamfer] Chamfer038
  Base = -> Fusion248002050204
  Edges = 2 edges r=3.99: [Edge8,Edge10]
FEATURE [Part::Chamfer] Chamfer039
  Base = -> Chamfer038
  Edges = 2 edges r=3.49: [Edge11,Edge14]
FEATURE [Part::Fillet] Fillet414
  Base = -> Chamfer039
  Edges = 2 edges r=2: [Edge14,Edge18]
FEATURE [Part::Cut] Cut014330
  Base = -> Fillet414
  Refine = true
  Tool = -> Cylinder1218
FEATURE [Part::MultiFuse] Fusion248002050207
  Refine = true
  Shapes = -> [Cut014330,Cut014292,Fillet413]
FEATURE [Part::Cut] Cut014331
  Base = -> Fusion248002050207
  Refine = true
  Tool = -> Cylinder1235
FEATURE [Part::Cut] Cut014332
  Base = -> Cut014331
  Refine = true
  Tool = -> Fusion248002050202
FEATURE [Part::Cut] Cut014333  label="bucket-body"
  Base = -> Cut014332
  Refine = true
  Tool = -> Fusion248002050194
FEATURE [Part::MultiFuse] Fusion248002050208
  Refine = true
  Shapes = -> [Box542,Fillet409]
FEATURE [Part::Cut] Cut014334
  Base = -> Fusion248002050208
  Refine = true
  Tool = -> Cylinder1275
FEATURE [Part::Cut] Cut014335
  Base = -> Cut014334
  Refine = true
  Tool = -> Fusion248002050197
FEATURE [Part::Cut] Cut014336
  Base = -> Cut014335
  Refine = true
  Tool = -> Cylinder1230
FEATURE [Part::Cut] Cut014337
  Base = -> Cut014336
  Refine = true
  Tool = -> Cut014272
FEATURE [Part::Fillet] Fillet415  label="bucket-rotating-motor-holder"
  Base = -> Cut014337
  Edges = 4 edges r=2: [Edge2,Edge4,Edge103,Edge105]
FEATURE [Part::Cylinder] Cylinder1334
  Angle = 77
  AttacherType = Attacher::AttachEngine3D
  Height = 60
  Placement = pos=(432,85,100) rot=(0,1,0;1.5708rad)
  Radius = 55
FEATURE [Part::Cylinder] Cylinder1335
  Angle = 80
  AttacherType = Attacher::AttachEngine3D
  Height = 56
  Placement = pos=(434,85,100) rot=(0,1,0;1.5708rad)
  Radius = 53
FEATURE [Part::Cut] Cut014338
  Base = -> Cylinder1334
  Refine = true
  Tool = -> Cylinder1335
FEATURE [Part::Chamfer] Chamfer040
  Base = -> Cut014338
  Edges = 1 edges: [Edge15 r1=1 r2=20]
FEATURE [Part::Cylinder] Cylinder1336
  Angle = 360
  AttacherType = Attacher::AttachEngine3D
  Height = 2.5
  Placement = pos=(434,102.5,100) rot=(0,1,0;1.5708rad)
  Radius = 3.5
FEATURE [Part::Cylinder] Cylinder1337
  Angle = 360
  AttacherType = Attacher::AttachEngine3D
  Height = 2.5
  Placement = pos=(434,93.5,94) rot=(0,1,0;1.5708rad)
  Radius = 3.5
FEATURE [Part::MultiFuse] Fusion248002050209
  Refine = true
  Shapes = -> [Cylinder1337,Cylinder1336]
FEATURE [Part::Cylinder] Cylinder1338
  Angle = 360
  AttacherType = Attacher::AttachEngine3D
  Height = 2.5
  Placement = pos=(435,102.5,100) rot=(0,1,0;1.5708rad)
  Radius = 3.5
FEATURE [Part::Cylinder] Cylinder1339
  Angle = 360
  AttacherType = Attacher::AttachEngine3D
  Height = 2.5
  Placement = pos=(435,93.5,94) rot=(0,1,0;1.5708rad)
  Radius = 3.5
FEATURE [Part::MultiFuse] Fusion248002050210
  Placement = pos=(52.5,0,0) rot=(0,0,1;0rad)
  Refine = true
  Shapes = -> [Cylinder1339,Cylinder1338]
FEATURE [Part::Cylinder] Cylinder1340
  Angle = 360
  AttacherType = Attacher::AttachEngine3D
  Height = 60
  Placement = pos=(432,103,100) rot=(0,1,0;1.5708rad)
  Radius = 1.5
FEATURE [Part::Cylinder] Cylinder1341
  Angle = 360
  AttacherType = Attacher::AttachEngine3D
  Height = 60
  Placement = pos=(432,94,94) rot=(0,1,0;1.5708rad)
  Radius = 1.5
FEATURE [Part::MultiFuse] Fusion248002050211
  Refine = true
  Shapes = -> [Cylinder1340,Cylinder1341]
FEATURE [Part::Cylinder] Cylinder1342  label="Cylinder1452"
  Angle = 360
  AttacherType = Attacher::AttachEngine3D
  Height = 10
  Placement = pos=(486,80.5,41.3) rot=(0,0,1;0rad)
  Radius = 1
FEATURE [Part::Cylinder] Cylinder1343  label="Cylinder1453"
  Angle = 360
  AttacherType = Attacher::AttachEngine3D
  Height = 10
  Placement = pos=(472,80.5,41.3) rot=(0,0,1;0rad)
  Radius = 1
FEATURE [Part::Cylinder] Cylinder1344  label="Cylinder1454"
  Angle = 360
  AttacherType = Attacher::AttachEngine3D
  Height = 10
  Placement = pos=(458,80.5,41.3) rot=(0,0,1;0rad)
  Radius = 1
FEATURE [Part::Cylinder] Cylinder1345  label="Cylinder1455"
  Angle = 360
  AttacherType = Attacher::AttachEngine3D
  Height = 10
  Placement = pos=(444,80.5,41.3) rot=(0,0,1;0rad)
  Radius = 1
FEATURE [Part::MultiFuse] Fusion248002050212
  Placement = pos=(-7,9,0) rot=(0,0,1;0rad)
  Refine = true
  Shapes = -> [Cylinder1345,Cylinder1343,Cylinder1344,Cylinder1342]
FEATURE [Part::Feature] Face004
  shape: bbox 2e-07 x 61.83 x 28.12 mm, 1 faces, 0 solids (baked)
FEATURE [Part::Extrusion] Extrude004
  Base = -> Face004
  Dir = (-2,0,0)
  DirMode = 0
  FaceMakerClass = Part::FaceMakerExtrusion
  LengthFwd = 0
  LengthRev = 0
  Solid = true
  Symmetric = false
FEATURE [Part::Feature] Face005
  shape: bbox 2e-07 x 61.83 x 28.12 mm, 1 faces, 0 solids (baked)
FEATURE [Part::Extrusion] Extrude005
  Base = -> Face005
  Dir = (-2,0,0)
  DirMode = 0
  FaceMakerClass = Part::FaceMakerExtrusion
  LengthFwd = 0
  LengthRev = 0
  Placement = pos=(-58,0,0) rot=(0,0,1;0rad)
  Solid = true
  Symmetric = false
FEATURE [Part::Cylinder] Cylinder1346  label="Cylinder1456"
  Angle = 360
  AttacherType = Attacher::AttachEngine3D
  Height = 10
  Placement = pos=(486,80.5,41.3) rot=(0,0,1;0rad)
  Radius = 1
FEATURE [Part::Cylinder] Cylinder1347  label="Cylinder1457"
  Angle = 360
  AttacherType = Attacher::AttachEngine3D
  Height = 10
  Placement = pos=(472,80.5,41.3) rot=(0,0,1;0rad)
  Radius = 1
FEATURE [Part::Cylinder] Cylinder1348  label="Cylinder1458"
  Angle = 360
  AttacherType = Attacher::AttachEngine3D
  Height = 10
  Placement = pos=(458,80.5,41.3) rot=(0,0,1;0rad)
  Radius = 1
FEATURE [Part::Cylinder] Cylinder1349  label="Cylinder1459"
  Angle = 360
  AttacherType = Attacher::AttachEngine3D
  Height = 10
  Placement = pos=(444,80.5,41.3) rot=(0,0,1;0rad)
  Radius = 1
FEATURE [Part::MultiFuse] Fusion248002050216
  Refine = true
  Shapes = -> [Cylinder1349,Cylinder1347,Cylinder1348,Cylinder1346]
FEATURE [Part::MultiFuse] Fusion248002050217
  Refine = true
  Shapes = -> [Fusion248002050209,Fusion248002050210]
FEATURE [Part::MultiFuse] Fusion248002050218
  Refine = true
  Shapes = -> [Chamfer040,Extrude004,Extrude005]
FEATURE [Part::Chamfer] Chamfer041
  Base = -> Fusion248002050217
  Edges = 4 edges r=1: [Edge1,Edge6,Edge9,Edge10]
FEATURE [Part::MultiFuse] Fusion248002050219
  Refine = true
  Shapes = -> [Fusion248002050218,Chamfer041]
FEATURE [Part::Chamfer] Chamfer042
  Base = -> Fusion248002050219
  Edges = 4 edges r=1.49: [Edge13,Edge32,Edge39,Edge48]
FEATURE [Part::Cut] Cut014339
  Base = -> Chamfer042
  Refine = true
  Tool = -> Fusion248002050211
FEATURE [Part::Fillet] Fillet416
  Base = -> Cut014339
  Edges = 6 edges r=12: [Edge24,Edge30,Edge32,Edge45,Edge73,Edge81]
FEATURE [Part::Cylinder] Cylinder1350
  Angle = 77
  AttacherType = Attacher::AttachEngine3D
  Height = 60
  Placement = pos=(432,85,100) rot=(0,1,0;1.5708rad)
  Radius = 55
FEATURE [Part::Cylinder] Cylinder1351
  Angle = 80
  AttacherType = Attacher::AttachEngine3D
  Height = 56
  Placement = pos=(434,85,100) rot=(0,1,0;1.5708rad)
  Radius = 53
FEATURE [Part::Cut] Cut014340
  Base = -> Cylinder1350
  Refine = true
  Tool = -> Cylinder1351
FEATURE [Part::Chamfer] Chamfer043
  Base = -> Cut014340
  Edges = 1 edges: [Edge15 r1=1 r2=20]
FEATURE [Part::Cylinder] Cylinder1352
  Angle = 360
  AttacherType = Attacher::AttachEngine3D
  Height = 2.5
  Placement = pos=(434,102.5,100) rot=(0,1,0;1.5708rad)
  Radius = 3.5
FEATURE [Part::Cylinder] Cylinder1353
  Angle = 360
  AttacherType = Attacher::AttachEngine3D
  Height = 2.5
  Placement = pos=(434,93.5,94) rot=(0,1,0;1.5708rad)
  Radius = 3.5
FEATURE [Part::MultiFuse] Fusion248002050220
  Refine = true
  Shapes = -> [Cylinder1353,Cylinder1352]
FEATURE [Part::Cylinder] Cylinder1354
  Angle = 360
  AttacherType = Attacher::AttachEngine3D
  Height = 2.5
  Placement = pos=(435,102.5,100) rot=(0,1,0;1.5708rad)
  Radius = 3.5
FEATURE [Part::Cylinder] Cylinder1355
  Angle = 360
  AttacherType = Attacher::AttachEngine3D
  Height = 2.5
  Placement = pos=(435,93.5,94) rot=(0,1,0;1.5708rad)
  Radius = 3.5
FEATURE [Part::MultiFuse] Fusion248002050221
  Placement = pos=(52.5,0,0) rot=(0,0,1;0rad)
  Refine = true
  Shapes = -> [Cylinder1355,Cylinder1354]
FEATURE [Part::Cylinder] Cylinder1356
  Angle = 360
  AttacherType = Attacher::AttachEngine3D
  Height = 60
  Placement = pos=(432,103,100) rot=(0,1,0;1.5708rad)
  Radius = 1.5
FEATURE [Part::Cylinder] Cylinder1357
  Angle = 360
  AttacherType = Attacher::AttachEngine3D
  Height = 60
  Placement = pos=(432,94,94) rot=(0,1,0;1.5708rad)
  Radius = 1.5
FEATURE [Part::MultiFuse] Fusion248002050222
  Refine = true
  Shapes = -> [Cylinder1356,Cylinder1357]
FEATURE [Part::Feature] Face006
  shape: bbox 2e-07 x 61.83 x 28.12 mm, 1 faces, 0 solids (baked)
FEATURE [Part::Extrusion] Extrude006
  Base = -> Face006
  Dir = (-2,0,0)
  DirMode = 0
  FaceMakerClass = Part::FaceMakerExtrusion
  LengthFwd = 0
  LengthRev = 0
  Solid = true
  Symmetric = false
FEATURE [Part::Feature] Face007
  shape: bbox 2e-07 x 61.83 x 28.12 mm, 1 faces, 0 solids (baked)
FEATURE [Part::Extrusion] Extrude007
  Base = -> Face007
  Dir = (-2,0,0)
  DirMode = 0
  FaceMakerClass = Part::FaceMakerExtrusion
  LengthFwd = 0
  LengthRev = 0
  Placement = pos=(-58,0,0) rot=(0,0,1;0rad)
  Solid = true
  Symmetric = false
FEATURE [Part::MultiFuse] Fusion248002050223
  Refine = true
  Shapes = -> [Fusion248002050220,Fusion248002050221]
FEATURE [Part::MultiFuse] Fusion248002050224
  Refine = true
  Shapes = -> [Chamfer043,Extrude006,Extrude007]
FEATURE [Part::Chamfer] Chamfer044
  Base = -> Fusion248002050223
  Edges = 4 edges r=1: [Edge1,Edge6,Edge9,Edge10]
FEATURE [Part::MultiFuse] Fusion248002050225
  Refine = true
  Shapes = -> [Fusion248002050224,Chamfer044]
FEATURE [Part::Chamfer] Chamfer045
  Base = -> Fusion248002050225
  Edges = 4 edges r=1.49: [Edge13,Edge32,Edge39,Edge48]
FEATURE [Part::Cut] Cut014341
  Base = -> Chamfer045
  Refine = true
  Tool = -> Fusion248002050222
FEATURE [Part::Fillet] Fillet417
  Base = -> Cut014341
  Edges = 6 edges r=12: [Edge24,Edge30,Edge32,Edge45,Edge73,Edge81]
FEATURE [Part::Mirroring] Part__Mirroring002  label="Fillet417 (Mirror #3)"
  Base = (0,0,0)
  Normal = (0,1,0)
  Placement = pos=(0,170,0) rot=(0,0,1;0rad)
  Source = -> Fillet417
FEATURE [Part::Cut] Cut014342  label="bucket-left-half-large"
  Base = -> Fillet416
  Refine = true
  Tool = -> Fusion248002050212
FEATURE [Part::Cut] Cut014343  label="bucket-right-half-large"
  Base = -> Part__Mirroring002
  Refine = true
  Tool = -> Fusion248002050216
FEATURE [Part::Cut] Cut
  Base = -> Box545
  Refine = true
  Tool = -> Fusion248002050201
FEATURE [Part::Cut] Cut014344  label="bucket-gears-HOLES"
  Base = -> Cut
  Refine = true
  Tool = -> Fusion248002050200
FEATURE [Part::Cylinder] Cylinder1358
  Angle = 77
  AttacherType = Attacher::AttachEngine3D
  Height = 60
  Placement = pos=(432,85,100) rot=(0,1,0;1.5708rad)
  Radius = 46
FEATURE [Part::Cylinder] Cylinder1359
  Angle = 80
  AttacherType = Attacher::AttachEngine3D
  Height = 56
  Placement = pos=(434,85,100) rot=(0,1,0;1.5708rad)
  Radius = 44
FEATURE [Part::Cut] Cut014345
  Base = -> Cylinder1358
  Refine = true
  Tool = -> Cylinder1359
FEATURE [Part::Cylinder] Cylinder1360
  Angle = 360
  AttacherType = Attacher::AttachEngine3D
  Height = 2.5
  Placement = pos=(434,102.5,100) rot=(0,1,0;1.5708rad)
  Radius = 3.5
FEATURE [Part::Cylinder] Cylinder1361
  Angle = 360
  AttacherType = Attacher::AttachEngine3D
  Height = 2.5
  Placement = pos=(434,93.5,94) rot=(0,1,0;1.5708rad)
  Radius = 3.5
FEATURE [Part::MultiFuse] Fusion248002050226
  Refine = true
  Shapes = -> [Cylinder1361,Cylinder1360]
FEATURE [Part::Cylinder] Cylinder1362
  Angle = 360
  AttacherType = Attacher::AttachEngine3D
  Height = 2.5
  Placement = pos=(435,102.5,100) rot=(0,1,0;1.5708rad)
  Radius = 3.5
FEATURE [Part::Cylinder] Cylinder1363
  Angle = 360
  AttacherType = Attacher::AttachEngine3D
  Height = 2.5
  Placement = pos=(435,93.5,94) rot=(0,1,0;1.5708rad)
  Radius = 3.5
FEATURE [Part::MultiFuse] Fusion248002050227
  Placement = pos=(52.5,0,0) rot=(0,0,1;0rad)
  Refine = true
  Shapes = -> [Cylinder1363,Cylinder1362]
FEATURE [Part::Cylinder] Cylinder1364
  Angle = 360
  AttacherType = Attacher::AttachEngine3D
  Height = 60
  Placement = pos=(432,103,100) rot=(0,1,0;1.5708rad)
  Radius = 1.5
FEATURE [Part::Cylinder] Cylinder1365
  Angle = 360
  AttacherType = Attacher::AttachEngine3D
  Height = 60
  Placement = pos=(432,94,94) rot=(0,1,0;1.5708rad)
  Radius = 1.5
FEATURE [Part::MultiFuse] Fusion248002050228
  Refine = true
  Shapes = -> [Cylinder1364,Cylinder1365]
FEATURE [Part::Cylinder] Cylinder1366  label="Cylinder1460"
  Angle = 360
  AttacherType = Attacher::AttachEngine3D
  Height = 10
  Placement = pos=(486,80.5,41.3) rot=(0,0,1;0rad)
  Radius = 1
FEATURE [Part::Cylinder] Cylinder1367  label="Cylinder1461"
  Angle = 360
  AttacherType = Attacher::AttachEngine3D
  Height = 10
  Placement = pos=(472,80.5,41.3) rot=(0,0,1;0rad)
  Radius = 1
FEATURE [Part::Cylinder] Cylinder1368  label="Cylinder1462"
  Angle = 360
  AttacherType = Attacher::AttachEngine3D
  Height = 10
  Placement = pos=(458,80.5,41.3) rot=(0,0,1;0rad)
  Radius = 1
FEATURE [Part::Cylinder] Cylinder1369  label="Cylinder1463"
  Angle = 360
  AttacherType = Attacher::AttachEngine3D
  Height = 10
  Placement = pos=(444,80.5,41.3) rot=(0,0,1;0rad)
  Radius = 1
FEATURE [Part::MultiFuse] Fusion248002050229
  Placement = pos=(-6.5,9,8) rot=(0,0,1;0rad)
  Refine = true
  Shapes = -> [Cylinder1369,Cylinder1367,Cylinder1368,Cylinder1366]
FEATURE [Part::MultiFuse] Fusion248002050230
  Refine = true
  Shapes = -> [Fusion248002050226,Fusion248002050227]
FEATURE [Part::Chamfer] Chamfer
  Base = -> Cut014345
  Edges = 1 edges: [Edge15 r1=1 r2=20]
FEATURE [Part::Chamfer] Chamfer046
  Base = -> Fusion248002050230
  Edges = 4 edges r=1.9: [Edge1,Edge6,Edge9,Edge10]
  Placement = pos=(0,0.5,0) rot=(0,0,1;0rad)
FEATURE [Part::Feature] Face
  shape: bbox 2e-07 x 51.37 x 23.62 mm, 1 faces, 0 solids (baked)
FEATURE [Part::Extrusion] Extrude
  Base = -> Face
  Dir = (2,0,0)
  DirMode = 0
  FaceMakerClass = Part::FaceMakerExtrusion
  LengthFwd = 0
  LengthRev = 0
  Solid = true
  Symmetric = false
FEATURE [Part::Feature] Face008
  shape: bbox 2e-07 x 51.37 x 23.62 mm, 1 faces, 0 solids (baked)
FEATURE [Part::Extrusion] Extrude008
  Base = -> Face008
  Dir = (2,0,0)
  DirMode = 0
  FaceMakerClass = Part::FaceMakerExtrusion
  LengthFwd = 0
  LengthRev = 0
  Placement = pos=(58,0,0) rot=(0,0,1;0rad)
  Solid = true
  Symmetric = false
FEATURE [Part::MultiFuse] Fusion248002050231
  Refine = true
  Shapes = -> [Extrude008,Extrude,Chamfer]
FEATURE [Part::MultiFuse] Fusion248002050232
  Refine = true
  Shapes = -> [Chamfer046,Fusion248002050231]
FEATURE [Part::Chamfer] Chamfer047
  Base = -> Fusion248002050232
  Edges = 4 edges r=0.59: [Edge5,Edge20,Edge29,Edge50]
FEATURE [Part::Cut] Cut014346
  Base = -> Chamfer047
  Refine = true
  Tool = -> Fusion248002050228
FEATURE [Part::Chamfer] Chamfer048
  Base = -> Cut014346
  Edges = 2 edges r=5: [Edge37,Edge42]
FEATURE [Part::Fillet] Fillet418
  Base = -> Chamfer048
  Edges = 6 edges r=10: [Edge22,Edge61,Edge67,Edge68,Edge80,Edge101]
FEATURE [Part::Cylinder] Cylinder1370
  Angle = 77
  AttacherType = Attacher::AttachEngine3D
  Height = 60
  Placement = pos=(432,85,100) rot=(0,1,0;1.5708rad)
  Radius = 46
FEATURE [Part::Cylinder] Cylinder1371
  Angle = 80
  AttacherType = Attacher::AttachEngine3D
  Height = 56
  Placement = pos=(434,85,100) rot=(0,1,0;1.5708rad)
  Radius = 44
FEATURE [Part::Cut] Cut014347
  Base = -> Cylinder1370
  Refine = true
  Tool = -> Cylinder1371
FEATURE [Part::Cylinder] Cylinder1372
  Angle = 360
  AttacherType = Attacher::AttachEngine3D
  Height = 2.5
  Placement = pos=(434,102.5,100) rot=(0,1,0;1.5708rad)
  Radius = 3.5
FEATURE [Part::Cylinder] Cylinder1373
  Angle = 360
  AttacherType = Attacher::AttachEngine3D
  Height = 2.5
  Placement = pos=(434,93.5,94) rot=(0,1,0;1.5708rad)
  Radius = 3.5
FEATURE [Part::MultiFuse] Fusion248002050233
  Refine = true
  Shapes = -> [Cylinder1373,Cylinder1372]
FEATURE [Part::Cylinder] Cylinder1374
  Angle = 360
  AttacherType = Attacher::AttachEngine3D
  Height = 2.5
  Placement = pos=(435,102.5,100) rot=(0,1,0;1.5708rad)
  Radius = 3.5
FEATURE [Part::Cylinder] Cylinder1375
  Angle = 360
  AttacherType = Attacher::AttachEngine3D
  Height = 2.5
  Placement = pos=(435,93.5,94) rot=(0,1,0;1.5708rad)
  Radius = 3.5
FEATURE [Part::MultiFuse] Fusion248002050234
  Placement = pos=(52.5,0,0) rot=(0,0,1;0rad)
  Refine = true
  Shapes = -> [Cylinder1375,Cylinder1374]
FEATURE [Part::Cylinder] Cylinder1376
  Angle = 360
  AttacherType = Attacher::AttachEngine3D
  Height = 60
  Placement = pos=(432,103,100) rot=(0,1,0;1.5708rad)
  Radius = 1.5
FEATURE [Part::Cylinder] Cylinder1377
  Angle = 360
  AttacherType = Attacher::AttachEngine3D
  Height = 60
  Placement = pos=(432,94,94) rot=(0,1,0;1.5708rad)
  Radius = 1.5
FEATURE [Part::MultiFuse] Fusion248002050235
  Refine = true
  Shapes = -> [Cylinder1376,Cylinder1377]
FEATURE [Part::MultiFuse] Fusion248002050236
  Refine = true
  Shapes = -> [Fusion248002050233,Fusion248002050234]
FEATURE [Part::Chamfer] Chamfer049
  Base = -> Cut014347
  Edges = 1 edges: [Edge15 r1=1 r2=20]
FEATURE [Part::Chamfer] Chamfer050
  Base = -> Fusion248002050236
  Edges = 4 edges r=1.9: [Edge1,Edge6,Edge9,Edge10]
  Placement = pos=(0,0.5,0) rot=(0,0,1;0rad)
FEATURE [Part::Feature] Face009
  shape: bbox 2e-07 x 51.37 x 23.62 mm, 1 faces, 0 solids (baked)
FEATURE [Part::Extrusion] Extrude009
  Base = -> Face009
  Dir = (2,0,0)
  DirMode = 0
  FaceMakerClass = Part::FaceMakerExtrusion
  LengthFwd = 0
  LengthRev = 0
  Solid = true
  Symmetric = false
FEATURE [Part::Feature] Face010
  shape: bbox 2e-07 x 51.37 x 23.62 mm, 1 faces, 0 solids (baked)
FEATURE [Part::Extrusion] Extrude010
  Base = -> Face010
  Dir = (2,0,0)
  DirMode = 0
  FaceMakerClass = Part::FaceMakerExtrusion
  LengthFwd = 0
  LengthRev = 0
  Placement = pos=(58,0,0) rot=(0,0,1;0rad)
  Solid = true
  Symmetric = false
FEATURE [Part::MultiFuse] Fusion248002050237
  Refine = true
  Shapes = -> [Extrude010,Extrude009,Chamfer049]
FEATURE [Part::MultiFuse] Fusion248002050238
  Refine = true
  Shapes = -> [Chamfer050,Fusion248002050237]
FEATURE [Part::Chamfer] Chamfer051
  Base = -> Fusion248002050238
  Edges = 4 edges r=0.59: [Edge5,Edge20,Edge29,Edge50]
FEATURE [Part::Cut] Cut014348
  Base = -> Chamfer051
  Refine = true
  Tool = -> Fusion248002050235
FEATURE [Part::Chamfer] Chamfer052
  Base = -> Cut014348
  Edges = 2 edges r=5: [Edge37,Edge42]
FEATURE [Part::Fillet] Fillet419
  Base = -> Chamfer052
  Edges = 6 edges r=10: [Edge22,Edge61,Edge67,Edge68,Edge80,Edge101]
FEATURE [Part::Mirroring] Part__Mirroring003  label="Fillet419 (Mirror #3)"
  Base = (0,0,0)
  Normal = (0,1,0)
  Placement = pos=(0,170,0) rot=(0,0,1;0rad)
  Source = -> Fillet419
FEATURE [Part::MultiFuse] Fusion248002050239
  Refine = true
  Shapes = -> [Chamfer013,Chamfer015,Chamfer019,Chamfer017]
FEATURE [Part::Box] Box546  label="Cube772"
  AttacherType = Attacher::AttachEngine3D
  Height = 6
  Length = 5
  Placement = pos=(434,78,42) rot=(0,0,1;0rad)
  Width = 20
FEATURE [Part::Cylinder] Cylinder1378
  Angle = 80
  AttacherType = Attacher::AttachEngine3D
  Height = 60
  Placement = pos=(432,85,100) rot=(0,1,0;1.5708rad)
  Radius = 55
FEATURE [Part::Box] Box547  label="Cube773"
  AttacherType = Attacher::AttachEngine3D
  Height = 6
  Length = 10
  Placement = pos=(434,65,44.75) rot=(0,0,1;0rad)
  Width = 20
FEATURE [Part::MultiFuse] Fusion248002050240
  Refine = true
  Shapes = -> [Box547,Cylinder1378]
FEATURE [Part::Cut] Cut014349
  Base = -> Box546
  Refine = true
  Tool = -> Fusion248002050240
FEATURE [Part::Chamfer] Chamfer053
  Base = -> Cut014349
  Edges = 1 edges: [Edge17 r1=3 r2=8]
FEATURE [Part::Chamfer] Chamfer054
  Base = -> Chamfer053
  Edges = 1 edges: [Edge15 r1=11 r2=2]
  Placement = pos=(1,0,9) rot=(0,0,1;0rad)
FEATURE [Part::Box] Box548  label="Cube774"
  AttacherType = Attacher::AttachEngine3D
  Height = 6
  Length = 5
  Placement = pos=(434,78,42) rot=(0,0,1;0rad)
  Width = 20
FEATURE [Part::Cylinder] Cylinder1379
  Angle = 80
  AttacherType = Attacher::AttachEngine3D
  Height = 60
  Placement = pos=(432,85,100) rot=(0,1,0;1.5708rad)
  Radius = 55
FEATURE [Part::Box] Box549  label="Cube775"
  AttacherType = Attacher::AttachEngine3D
  Height = 6
  Length = 10
  Placement = pos=(434,65,44.75) rot=(0,0,1;0rad)
  Width = 20
FEATURE [Part::MultiFuse] Fusion248002050241
  Refine = true
  Shapes = -> [Box549,Cylinder1379]
FEATURE [Part::Cut] Cut014350
  Base = -> Box548
  Refine = true
  Tool = -> Fusion248002050241
FEATURE [Part::Chamfer] Chamfer055
  Base = -> Cut014350
  Edges = 1 edges: [Edge17 r1=3 r2=8]
FEATURE [Part::Chamfer] Chamfer056
  Base = -> Chamfer055
  Edges = 1 edges: [Edge15 r1=11 r2=2]
  Placement = pos=(29,0,9) rot=(0,0,1;0rad)
FEATURE [Part::Box] Box550  label="Cube776"
  AttacherType = Attacher::AttachEngine3D
  Height = 6
  Length = 5
  Placement = pos=(434,78,42) rot=(0,0,1;0rad)
  Width = 20
FEATURE [Part::Cylinder] Cylinder1380
  Angle = 80
  AttacherType = Attacher::AttachEngine3D
  Height = 60
  Placement = pos=(432,85,100) rot=(0,1,0;1.5708rad)
  Radius = 55
FEATURE [Part::Box] Box551  label="Cube777"
  AttacherType = Attacher::AttachEngine3D
  Height = 6
  Length = 10
  Placement = pos=(434,65,44.75) rot=(0,0,1;0rad)
  Width = 20
FEATURE [Part::MultiFuse] Fusion248002050242
  Refine = true
  Shapes = -> [Box551,Cylinder1380]
FEATURE [Part::Cut] Cut014351
  Base = -> Box550
  Refine = true
  Tool = -> Fusion248002050242
FEATURE [Part::Chamfer] Chamfer057
  Base = -> Cut014351
  Edges = 1 edges: [Edge17 r1=3 r2=8]
FEATURE [Part::Chamfer] Chamfer058
  Base = -> Chamfer057
  Edges = 1 edges: [Edge15 r1=11 r2=2]
  Placement = pos=(15,0,9) rot=(0,0,1;0rad)
FEATURE [Part::Box] Box552  label="Cube778"
  AttacherType = Attacher::AttachEngine3D
  Height = 6
  Length = 5
  Placement = pos=(434,78,42) rot=(0,0,1;0rad)
  Width = 20
FEATURE [Part::Cylinder] Cylinder1381
  Angle = 80
  AttacherType = Attacher::AttachEngine3D
  Height = 60
  Placement = pos=(432,85,100) rot=(0,1,0;1.5708rad)
  Radius = 55
FEATURE [Part::Box] Box553  label="Cube779"
  AttacherType = Attacher::AttachEngine3D
  Height = 6
  Length = 10
  Placement = pos=(434,65,44.75) rot=(0,0,1;0rad)
  Width = 20
FEATURE [Part::MultiFuse] Fusion248002050243
  Refine = true
  Shapes = -> [Box553,Cylinder1381]
FEATURE [Part::Cut] Cut014352
  Base = -> Box552
  Refine = true
  Tool = -> Fusion248002050243
FEATURE [Part::Chamfer] Chamfer059
  Base = -> Cut014352
  Edges = 1 edges: [Edge17 r1=3 r2=8]
FEATURE [Part::Chamfer] Chamfer060
  Base = -> Chamfer059
  Edges = 1 edges: [Edge15 r1=11 r2=2]
  Placement = pos=(43,0,9) rot=(0,0,1;0rad)
FEATURE [Part::MultiFuse] Fusion248002050244
  Refine = true
  Shapes = -> [Chamfer054,Chamfer056,Chamfer060,Chamfer058]
FEATURE [Part::Mirroring] Part__Mirroring  label="Fusion248002050244 (Mirror #3)"
  Base = (0,0,0)
  Normal = (0,1,0)
  Placement = pos=(7,170,0) rot=(0,0,1;0rad)
  Source = -> Fusion248002050244
FEATURE [Part::Cylinder] Cylinder1382  label="Cylinder1464"
  Angle = 360
  AttacherType = Attacher::AttachEngine3D
  Height = 10
  Placement = pos=(486,80.5,41.3) rot=(0,0,1;0rad)
  Radius = 1
FEATURE [Part::Cylinder] Cylinder1383  label="Cylinder1465"
  Angle = 360
  AttacherType = Attacher::AttachEngine3D
  Height = 10
  Placement = pos=(472,80.5,41.3) rot=(0,0,1;0rad)
  Radius = 1
FEATURE [Part::Cylinder] Cylinder1384  label="Cylinder1466"
  Angle = 360
  AttacherType = Attacher::AttachEngine3D
  Height = 10
  Placement = pos=(458,80.5,41.3) rot=(0,0,1;0rad)
  Radius = 1
FEATURE [Part::Cylinder] Cylinder1385  label="Cylinder1467"
  Angle = 360
  AttacherType = Attacher::AttachEngine3D
  Height = 10
  Placement = pos=(444,80.5,41.3) rot=(0,0,1;0rad)
  Radius = 1
FEATURE [Part::MultiFuse] Fusion248002050245
  Placement = pos=(0.5,0,8) rot=(0,0,1;0rad)
  Refine = true
  Shapes = -> [Cylinder1385,Cylinder1383,Cylinder1384,Cylinder1382]
FEATURE [Part::Cut] Cut014353  label="bucket-left-half"
  Base = -> Fillet418
  Placement = pos=(-1,0,0) rot=(0,0,1;0rad)
  Refine = true
  Tool = -> Fusion248002050229
FEATURE [Part::Cut] Cut014354  label="bucket-right-half"
  Base = -> Part__Mirroring003
  Placement = pos=(-1,0,0) rot=(0,0,1;0rad)
  Refine = true
  Tool = -> Fusion248002050245
FEATURE [Part::Cylinder] Cylinder1386
  Angle = 360
  AttacherType = Attacher::AttachEngine3D
  Height = 1
  Placement = pos=(436,103,100) rot=(0,1,0;1.5708rad)
  Radius = 3.5
FEATURE [Part::Cylinder] Cylinder1387
  Angle = 360
  AttacherType = Attacher::AttachEngine3D
  Height = 1
  Placement = pos=(436,67,100) rot=(0,1,0;1.5708rad)
  Radius = 3.5
FEATURE [Part::Cylinder] Cylinder1388
  Angle = 360
  AttacherType = Attacher::AttachEngine3D
  Height = 1
  Placement = pos=(436,103,100) rot=(0,1,0;1.5708rad)
  Radius = 1.7
FEATURE [Part::Cut] Cut014355  label="bucket-left-half-short-spacer"
  Base = -> Cylinder1386
  Placement = pos=(-0.5,0,0) rot=(0,0,1;0rad)
  Refine = true
  Tool = -> Cylinder1388
FEATURE [Part::Cylinder] Cylinder1389
  Angle = 360
  AttacherType = Attacher::AttachEngine3D
  Height = 1
  Placement = pos=(436,67,100) rot=(0,1,0;1.5708rad)
  Radius = 1.7
FEATURE [Part::Cut] Cut014356  label="bucket-right-half-short-spacer"
  Base = -> Cylinder1387
  Placement = pos=(-0.5,0,0) rot=(0,0,1;0rad)
  Refine = true
  Tool = -> Cylinder1389
FEATURE [Part::Cylinder] Cylinder1390
  Angle = 360
  AttacherType = Attacher::AttachEngine3D
  Height = 8.5
  Placement = pos=(436,103,100) rot=(0,1,0;1.5708rad)
  Radius = 3.5
FEATURE [Part::Cylinder] Cylinder1391
  Angle = 360
  AttacherType = Attacher::AttachEngine3D
  Height = 8.5
  Placement = pos=(436,67,100) rot=(0,1,0;1.5708rad)
  Radius = 3.5
FEATURE [Part::Cylinder] Cylinder1392
  Angle = 360
  AttacherType = Attacher::AttachEngine3D
  Height = 8.5
  Placement = pos=(436,103,100) rot=(0,1,0;1.5708rad)
  Radius = 1.7
FEATURE [Part::Cut] Cut014357  label="bucket-left-half-long-spacer"
  Base = -> Cylinder1390
  Placement = pos=(42,0,0) rot=(0,0,1;0rad)
  Refine = true
  Tool = -> Cylinder1392
FEATURE [Part::Cylinder] Cylinder1393
  Angle = 360
  AttacherType = Attacher::AttachEngine3D
  Height = 8.5
  Placement = pos=(436,67,100) rot=(0,1,0;1.5708rad)
  Radius = 1.7
FEATURE [Part::Cut] Cut014358  label="bucket-right-half-long-spacer"
  Base = -> Cylinder1391
  Placement = pos=(42,0,0) rot=(0,0,1;0rad)
  Refine = true
  Tool = -> Cylinder1393
FEATURE [Part::Cylinder] Cylinder1394
  Angle = 360
  AttacherType = Attacher::AttachEngine3D
  Height = 60
  Placement = pos=(432,103,100) rot=(0,1,0;1.5708rad)
  Radius = 1.5
FEATURE [Part::Cylinder] Cylinder1395
  Angle = 360
  AttacherType = Attacher::AttachEngine3D
  Height = 60
  Placement = pos=(432,94,94) rot=(0,1,0;1.5708rad)
  Radius = 1.5
FEATURE [Part::MultiFuse] Fusion248002050246
  Placement = pos=(-1,0,0) rot=(0,0,1;0rad)
  Refine = true
  Shapes = -> [Cylinder1394,Cylinder1395]
FEATURE [Part::Feature] Fusion248002050246001  label="Fusion248002050247"
  Placement = pos=(-1,0,0) rot=(0,0,1;0rad)
  shape: bbox 60 x 12 x 9 mm, 6 faces, 2 solids (baked)
FEATURE [Part::Mirroring] Part__Mirroring004  label="Fusion248002050247 (Mirror #4)"
  Base = (0,0,0)
  Normal = (0,1,0)
  Placement = pos=(0,170,0) rot=(0,0,1;0rad)
  Source = -> Fusion248002050246001
FEATURE [Part::MultiFuse] Fusion248002050246002
  Refine = true
  Shapes = -> [Fusion248002050246,Part__Mirroring004]
FEATURE [Part::Feature] Fusion248002050246002001  label="Fusion248002050246003"
  shape: bbox 60 x 39 x 9 mm, 12 faces, 4 solids (baked)
FEATURE [Part::Feature] Fusion248002050246002002  label="Fusion248002050246004"
  shape: bbox 60 x 39 x 9 mm, 12 faces, 4 solids (baked)
FEATURE [Part::Cut] Cut014359
  Base = -> Fusion
  Refine = true
  Tool = -> Fusion248002050246002001
FEATURE [Part::Cut] Cut014360
  Base = -> Fusion248002050123
  Refine = true
  Tool = -> Fusion248002050246002002
